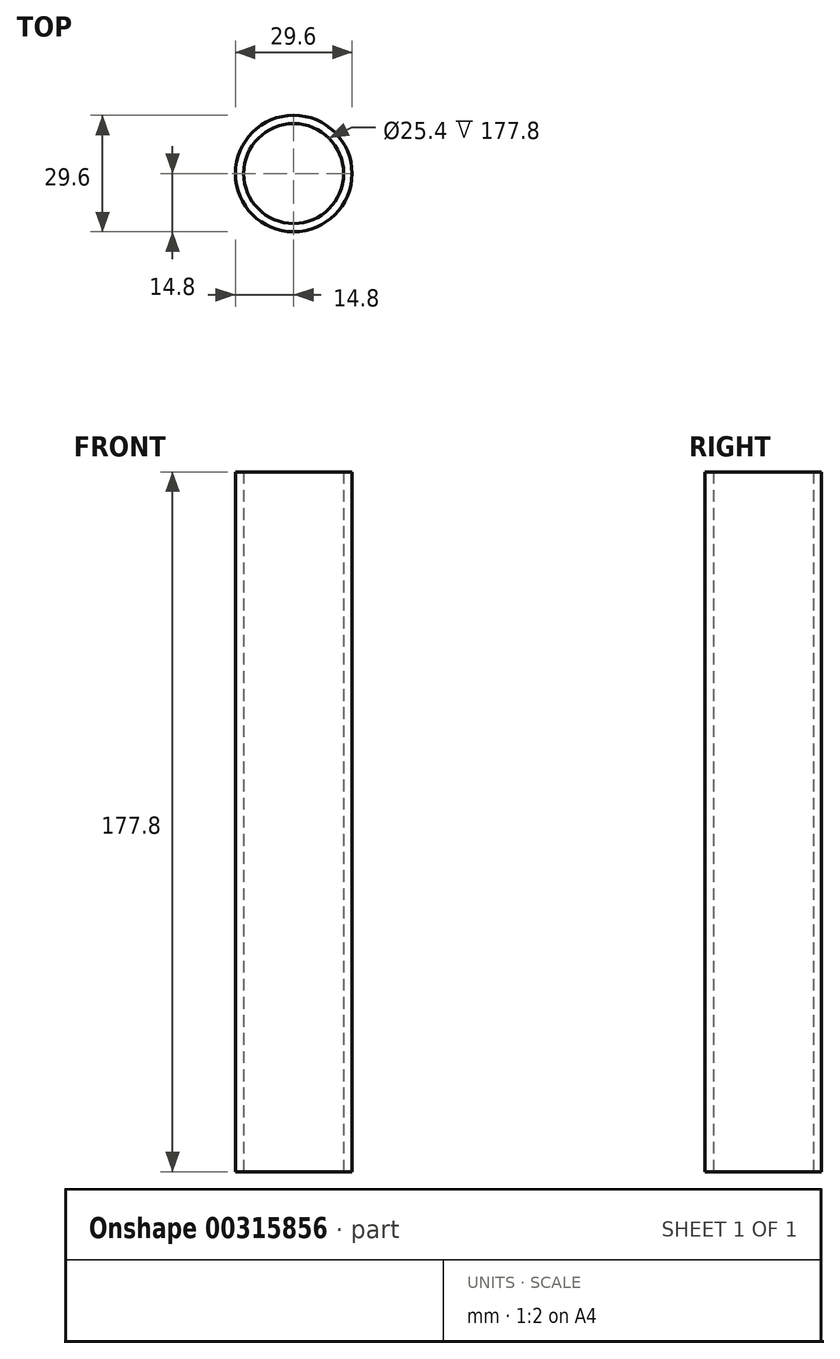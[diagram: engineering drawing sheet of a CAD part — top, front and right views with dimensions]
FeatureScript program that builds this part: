
annotation { "Feature Type Name" : "Feature", "Feature Type Description" : "" }
export const myFeature = defineFeature(function(context is Context, id is Id, definition is map)
    precondition{}
    {
        {
            var Q0;
            Q0=qCreatedBy(makeId("Top.planeOp"),FACE);
            var sketch = newSketch(context, id + "F0", { "sketchPlane" : qUnion([Q0])});
            skCircle(sketch, "E0", {"center": v(0, 0) * mm, "radius": 14.8 * mm});
            skCircle(sketch, "E1", {"center": v(0, 0) * mm, "radius": 12.7 * mm});
            skSolve(sketch);
        }
        {
            var Q0;
            Q0=makeQuery(id+"F0.imprint","IMPRINT",FACE,{"disambiguationData":[TD([[makeQuery(id+"F0.imprint","IMPRINT",EDGE,{"derivedFrom":sQuery(id+"F0.wireOp",EDGE,"E0")}),1.0]])]});
            extrude(context, id + "F1", {"entities" : qUnion([Q0]), "endBound" : BoundingType.SYMMETRIC, "depth" : 177.8 * mm});
        }
    });
